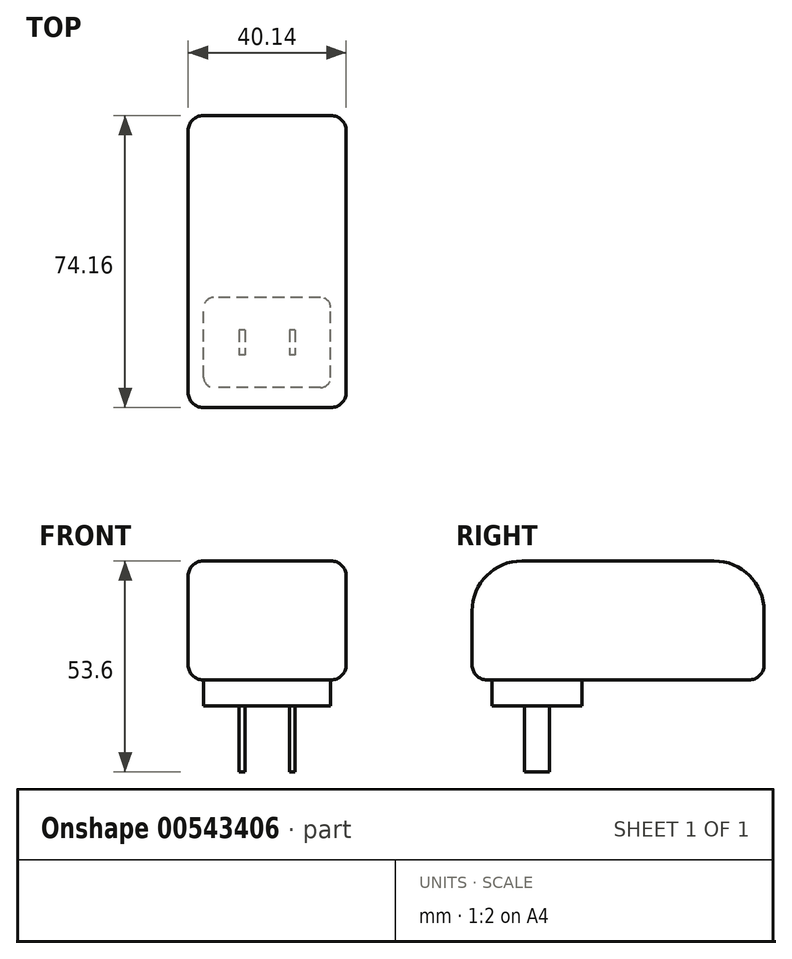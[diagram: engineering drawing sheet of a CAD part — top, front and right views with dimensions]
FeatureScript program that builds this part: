
annotation { "Feature Type Name" : "Feature", "Feature Type Description" : "" }
export const myFeature = defineFeature(function(context is Context, id is Id, definition is map)
    precondition{}
    {
        {
            var Q0;
            Q0=qCreatedBy(makeId("Right.planeOp"),FACE);
            var sketch = newSketch(context, id + "F0", { "sketchPlane" : qUnion([Q0])});
            skLineSegment(sketch, "E0.bottom", {"start": v(-37.08, 0) * mm, "end": v(37.08, 0) * mm});
            skLineSegment(sketch, "E0.top", {"start": v(-24.38, 30.23) * mm, "end": v(24.38, 30.23) * mm});
            skLineSegment(sketch, "E0.left", {"start": v(-37.08, 0) * mm, "end": v(-37.08, 17.53) * mm});
            skLineSegment(sketch, "E0.right", {"start": v(37.08, 0) * mm, "end": v(37.08, 17.53) * mm});
            skPoint(sketch, "E1.visualSharp", {"position": v(-37.08, 30.23) * mm});
            skArc(sketch, "E1.filletArc", {"start": v(-24.38, 30.23) * mm, "mid": v(-33.36, 26.5) * mm, "end": v(-37.08, 17.53) * mm});
            skPoint(sketch, "E2.visualSharp", {"position": v(37.08, 30.23) * mm});
            skArc(sketch, "E2.filletArc", {"start": v(37.08, 17.53) * mm, "mid": v(33.36, 26.5) * mm, "end": v(24.38, 30.23) * mm});
            skSolve(sketch);
        }
        {
            var Q0;
            Q0 = qSketchRegion(id + "F0", true);
            extrude(context, id + "F1", {"entities" : qUnion([Q0]), "endBound" : BoundingType.SYMMETRIC, "depth" : 40.13 * mm, "offsetDistance" : 25.4 * mm});
        }
        {
            var Q0;
            Q0=makeQuery(id+"F1.opExtrude","CAP_EDGE",EDGE,{"disambiguationData":[OSD([sQuery(id+"F0.wireOp",EDGE,"E0.top")])],"isStart":false});
            var Q1;
            Q1=makeQuery(id+"F1.opExtrude","CAP_EDGE",EDGE,{"disambiguationData":[OSD([sQuery(id+"F0.wireOp",EDGE,"E0.top")])],"isStart":true});
            var Q2;
            Q2=makeQuery(id+"F1.opExtrude","SWEPT_EDGE",EDGE,{"disambiguationData":[OSD([sQuery(id+"F0.wireOp",EDGE,"E0.bottom"),sQuery(id+"F0.wireOp",EDGE,"E0.left")])]});
            var Q3;
            Q3=makeQuery(id+"F1.opExtrude","CAP_EDGE",EDGE,{"disambiguationData":[OSD([sQuery(id+"F0.wireOp",EDGE,"E0.bottom")])],"isStart":false});
            var Q4;
            Q4=makeQuery(id+"F1.opExtrude","CAP_EDGE",EDGE,{"disambiguationData":[OSD([sQuery(id+"F0.wireOp",EDGE,"E0.bottom")])],"isStart":true});
            var Q5;
            Q5=makeQuery(id+"F1.opExtrude","SWEPT_EDGE",EDGE,{"disambiguationData":[OSD([sQuery(id+"F0.wireOp",EDGE,"E0.bottom"),sQuery(id+"F0.wireOp",EDGE,"E0.right")])]});
            fillet(context, id + "F2", {"entities" : qUnion([Q0, Q1, Q2, Q3, Q4, Q5]), "radius" : 3.8 * mm, "tangentPropagation" : true, "allowEdgeOverflow" : false});
        }
        {
            var Q0;
            Q0=makeQuery(id+"F1.opExtrude","SWEPT_FACE",FACE,{"disambiguationData":[OSD([sQuery(id+"F0.wireOp",EDGE,"E0.bottom")])]});
            var sketch = newSketch(context, id + "F3", { "sketchPlane" : qUnion([Q0])});
            skLineSegment(sketch, "E3.bottom", {"start": v(16.13, 32) * mm, "end": v(-16.13, 32) * mm});
            skLineSegment(sketch, "E3.top", {"start": v(16.13, 9.14) * mm, "end": v(-16.13, 9.14) * mm});
            skLineSegment(sketch, "E3.left", {"start": v(16.13, 32) * mm, "end": v(16.13, 9.14) * mm});
            skLineSegment(sketch, "E3.right", {"start": v(-16.13, 32) * mm, "end": v(-16.13, 9.14) * mm});
            skLineSegment(sketch, "E4", {"start": v(0, 57.47) * mm, "end": v(0, -43.98) * mm, "construction": true});
            skSolve(sketch);
        }
        {
            var Q0;
            Q0 = qSketchRegion(id + "F3", true);
            extrude(context, id + "F4", {"entities" : qUnion([Q0]), "operationType" : NewBodyOperationType.ADD, "depth" : 6.6 * mm, "offsetDistance" : 25.4 * mm});
        }
        {
            var Q0;
            Q0=makeQuery(id+"F4.opExtrude","SWEPT_EDGE",EDGE,{"disambiguationData":[OSD([sQuery(id+"F3.wireOp",EDGE,"E3.top"),sQuery(id+"F3.wireOp",EDGE,"E3.left")])]});
            var Q1;
            Q1=makeQuery(id+"F4.opExtrude","SWEPT_EDGE",EDGE,{"disambiguationData":[OSD([sQuery(id+"F3.wireOp",EDGE,"E3.bottom"),sQuery(id+"F3.wireOp",EDGE,"E3.left")])]});
            var Q2;
            Q2=makeQuery(id+"F4.opExtrude","SWEPT_EDGE",EDGE,{"disambiguationData":[OSD([sQuery(id+"F3.wireOp",EDGE,"E3.bottom"),sQuery(id+"F3.wireOp",EDGE,"E3.right")])]});
            var Q3;
            Q3=makeQuery(id+"F4.opExtrude","SWEPT_EDGE",EDGE,{"disambiguationData":[OSD([sQuery(id+"F3.wireOp",EDGE,"E3.top"),sQuery(id+"F3.wireOp",EDGE,"E3.right")])]});
            fillet(context, id + "F5", {"entities" : qUnion([Q0, Q1, Q2, Q3]), "radius" : 2.54 * mm, "tangentPropagation" : true, "allowEdgeOverflow" : false});
        }
        {
            var Q0;
            Q0=makeQuery(id+"F4.opExtrude","CAP_FACE",FACE,{"disambiguationData":[OSD([sQuery(id+"F3.wireOp",EDGE,"E3.bottom"),sQuery(id+"F3.wireOp",EDGE,"E3.top"),sQuery(id+"F3.wireOp",EDGE,"E3.left"),sQuery(id+"F3.wireOp",EDGE,"E3.right")])],"isStart":false});
            var sketch = newSketch(context, id + "F6", { "sketchPlane" : qUnion([Q0])});
            skLineSegment(sketch, "E5", {"start": v(16.13, 20.57) * mm, "end": v(-16.13, 20.57) * mm, "construction": true});
            skLineSegment(sketch, "E6.bottom", {"start": v(7.12, 17.4) * mm, "end": v(5.65, 17.4) * mm});
            skLineSegment(sketch, "E6.top", {"start": v(7.12, 23.75) * mm, "end": v(5.65, 23.75) * mm});
            skLineSegment(sketch, "E6.left", {"start": v(7.12, 17.4) * mm, "end": v(7.12, 23.75) * mm});
            skLineSegment(sketch, "E6.right", {"start": v(5.65, 17.4) * mm, "end": v(5.65, 23.75) * mm});
            skPoint(sketch, "E6.middle", {"position": v(6.39, 20.57) * mm});
            skLineSegment(sketch, "E7.bottom", {"start": v(-5.65, 17.4) * mm, "end": v(-7.12, 17.4) * mm});
            skLineSegment(sketch, "E7.top", {"start": v(-5.65, 23.75) * mm, "end": v(-7.12, 23.75) * mm});
            skLineSegment(sketch, "E7.left", {"start": v(-5.65, 17.4) * mm, "end": v(-5.65, 23.75) * mm});
            skLineSegment(sketch, "E7.right", {"start": v(-7.12, 17.4) * mm, "end": v(-7.12, 23.75) * mm});
            skPoint(sketch, "E7.middle", {"position": v(-6.39, 20.57) * mm});
            skLineSegment(sketch, "E8", {"start": v(0, 38.13) * mm, "end": v(0, 4.28) * mm, "construction": true});
            skSolve(sketch);
        }
        {
            var Q0;
            Q0 = qSketchRegion(id + "F6", true);
            extrude(context, id + "F7", {"entities" : qUnion([Q0]), "operationType" : NewBodyOperationType.ADD, "depth" : 16.76 * mm, "offsetDistance" : 25.4 * mm});
        }
    });
